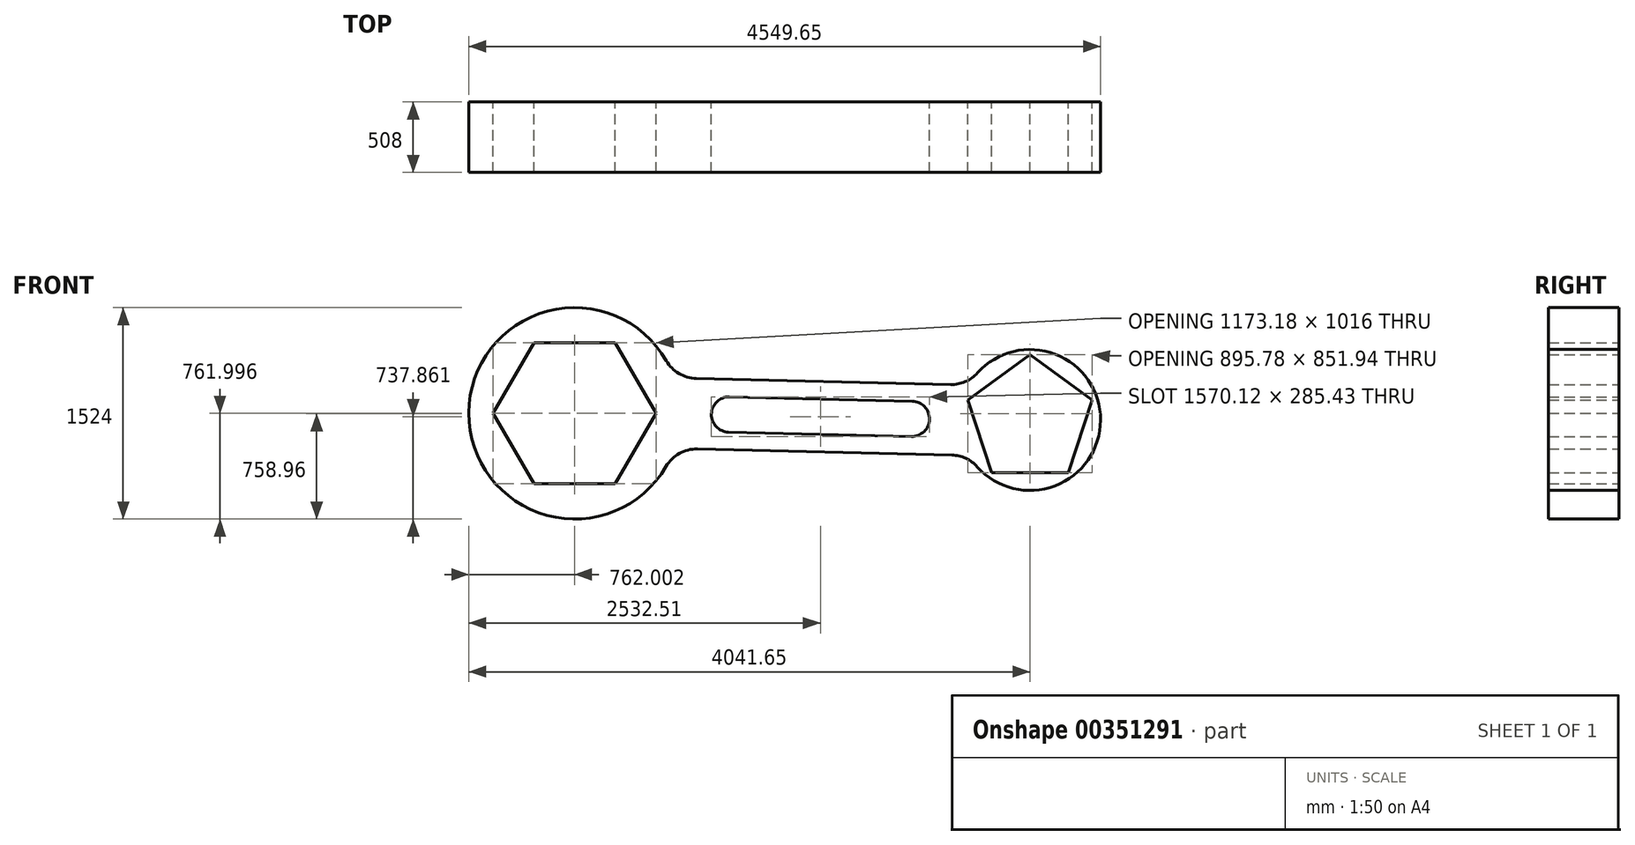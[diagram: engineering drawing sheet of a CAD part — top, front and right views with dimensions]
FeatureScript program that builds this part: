
annotation { "Feature Type Name" : "Feature", "Feature Type Description" : "" }
export const myFeature = defineFeature(function(context is Context, id is Id, definition is map)
    precondition{}
    {
        {
            var Q0;
            Q0=qCreatedBy(makeId("Front.planeOp"),FACE);
            var sketch = newSketch(context, id + "F0", { "sketchPlane" : qUnion([Q0])});
            skLineSegment(sketch, "E0", {"start": v(90.87, -26.94) * mm, "end": v(92.1, -26.94) * mm});
            skCircle(sketch, "E1", {"center": v(2609.74, -118.06) * mm, "radius": 508 * mm});
            skPoint(sketch, "E1.centerSnap0", {"position": v(2098.12, -118.06) * mm});
            skCircle(sketch, "E2", {"center": v(-669.9, -70.05) * mm, "radius": 762 * mm});
            skPoint(sketch, "E3.0.midPoint", {"position": v(-218.37, -404.57) * mm});
            skPoint(sketch, "E4.end.orphan", {"position": v(0, -26.94) * mm});
            skPoint(sketch, "E4.start.orphan", {"position": v(0, -290.75) * mm});
            skArc(sketch, "E5", {"start": v(445.54, 48.52) * mm, "mid": v(315.54, -75.4) * mm, "end": v(439.46, -205.4) * mm});
            skArc(sketch, "E6", {"start": v(1755.65, -236.9) * mm, "mid": v(1885.66, -112.98) * mm, "end": v(1761.73, 17.03) * mm});
            skLineSegment(sketch, "E7", {"start": v(445.54, 48.52) * mm, "end": v(1761.73, 17.03) * mm});
            skLineSegment(sketch, "E8", {"start": v(439.46, -205.4) * mm, "end": v(1755.65, -236.9) * mm});
            skCircle(sketch, "E9.cCircle", {"center": v(2609.74, -118.06) * mm, "radius": 381 * mm, "construction": true});
            skLineSegment(sketch, "E9.0", {"start": v(3057.64, 27.47) * mm, "end": v(2886.56, -499.06) * mm});
            skLineSegment(sketch, "E9.1", {"start": v(2886.56, -499.06) * mm, "end": v(2332.93, -499.06) * mm});
            skLineSegment(sketch, "E9.2", {"start": v(2332.93, -499.06) * mm, "end": v(2161.85, 27.47) * mm});
            skLineSegment(sketch, "E9.3", {"start": v(2161.85, 27.47) * mm, "end": v(2609.74, 352.88) * mm});
            skLineSegment(sketch, "E9.4", {"start": v(2609.74, 352.88) * mm, "end": v(3057.64, 27.47) * mm});
            skPoint(sketch, "E9.0.midPoint", {"position": v(2972.1, -235.8) * mm});
            skCircle(sketch, "E10.cCircle", {"center": v(-669.9, -70.05) * mm, "radius": 508 * mm, "construction": true});
            skLineSegment(sketch, "E10.0", {"start": v(-376.61, -578.05) * mm, "end": v(-963.2, -578.05) * mm});
            skLineSegment(sketch, "E10.1", {"start": v(-963.2, -578.05) * mm, "end": v(-1256.5, -70.05) * mm});
            skLineSegment(sketch, "E10.2", {"start": v(-1256.5, -70.05) * mm, "end": v(-963.2, 437.95) * mm});
            skLineSegment(sketch, "E10.3", {"start": v(-963.2, 437.95) * mm, "end": v(-376.61, 437.95) * mm});
            skLineSegment(sketch, "E10.4", {"start": v(-376.61, 437.95) * mm, "end": v(-83.32, -70.05) * mm});
            skLineSegment(sketch, "E10.5", {"start": v(-83.32, -70.05) * mm, "end": v(-376.61, -578.05) * mm});
            skPoint(sketch, "E10.0.midPoint", {"position": v(-669.9, -578.05) * mm});
            skLineSegment(sketch, "E11", {"start": v(2098.12, -118.06) * mm, "end": v(92.1, -70.05) * mm});
            skLineSegment(sketch, "E12", {"start": v(205.46, 181.3) * mm, "end": v(2037.02, 137.47) * mm});
            skLineSegment(sketch, "E13", {"start": v(214.36, -327.05) * mm, "end": v(2046.76, -370.9) * mm});
            skArc(sketch, "E14", {"start": v(-8.83, 308.91) * mm, "mid": v(81.58, 217) * mm, "end": v(205.46, 181.3) * mm});
            skArc(sketch, "E15", {"start": v(214.36, -327.05) * mm, "mid": v(84.29, -359.3) * mm, "end": v(-11.27, -453.25) * mm});
            skArc(sketch, "E16", {"start": v(2230.37, -455.9) * mm, "mid": v(2147.4, -394.34) * mm, "end": v(2046.76, -370.9) * mm});
            skArc(sketch, "E17", {"start": v(2037.02, 137.47) * mm, "mid": v(2143.7, 158.18) * mm, "end": v(2231.98, 221.58) * mm});
            skSolve(sketch);
        }
        {
            var Q0;
            Q0=makeQuery(id+"F0.imprint","IMPRINT",FACE,{"disambiguationData":[TD([[makeQuery(id+"F0.imprint","IMPRINT",EDGE,{"derivedFrom":sQuery(id+"F0.wireOp",EDGE,"E10.0")}),1.0]])]});
            var Q1;
            Q1=makeQuery(id+"F0.imprint","IMPRINT",FACE,{"disambiguationData":[TD([[makeQuery(id+"F0.imprint","IMPRINT",EDGE,{"derivedFrom":sQuery(id+"F0.wireOp",EDGE,"yFXfpv2J-3eob-FefI-qzjV-m2IyFrXhLOzh.bottom")}),-1.0]])]});
            var Q2;
            Q2=makeQuery(id+"F0.imprint","IMPRINT",FACE,{"disambiguationData":[TD([[makeQuery(id+"F0.imprint","IMPRINT",EDGE,{"derivedFrom":sQuery(id+"F0.wireOp",EDGE,"E9.0")}),1.0]])]});
            var Q3;
            {var subQ0=sQuery(id+"F0.wireOp",EDGE,"E7");Q3=makeQuery(id+"F0.imprint","IMPRINT",FACE,{"disambiguationData":[TD([[makeQuery(id+"F0.imprint","IMPRINT",EDGE,{"derivedFrom":subQ0}),1.0]])]});}
            extrude(context, id + "F1", {"entities" : qUnion([Q0, Q1, Q2, Q3]), "depth" : 508 * mm});
        }
    });
